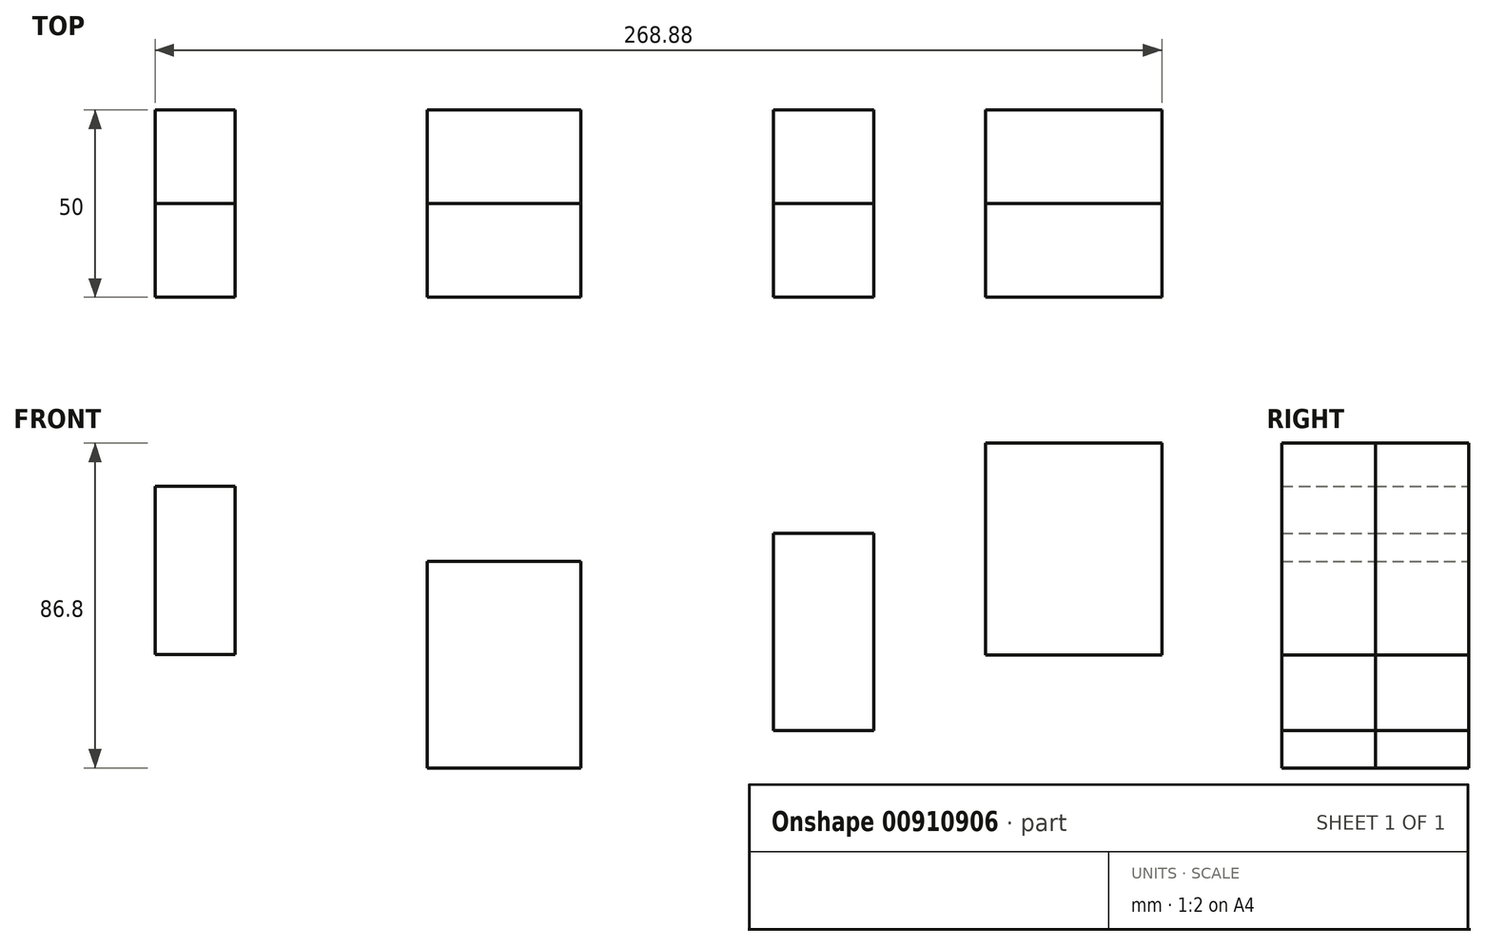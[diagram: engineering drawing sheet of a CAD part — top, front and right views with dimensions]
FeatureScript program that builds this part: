
annotation { "Feature Type Name" : "Feature", "Feature Type Description" : "" }
export const myFeature = defineFeature(function(context is Context, id is Id, definition is map)
    precondition{}
    {
        {
            var Q0;
            Q0=qCreatedBy(makeId("Front.planeOp"),FACE);
            var sketch = newSketch(context, id + "F0", { "sketchPlane" : qUnion([Q0])});
            skLineSegment(sketch, "E0.bottom", {"start": v(-124.32, 42.1) * mm, "end": v(-102.93, 42.1) * mm});
            skLineSegment(sketch, "E0.top", {"start": v(-124.32, -2.77) * mm, "end": v(-102.93, -2.77) * mm});
            skLineSegment(sketch, "E0.left", {"start": v(-124.32, 42.1) * mm, "end": v(-124.32, -2.77) * mm});
            skLineSegment(sketch, "E0.right", {"start": v(-102.93, 42.1) * mm, "end": v(-102.93, -2.77) * mm});
            skLineSegment(sketch, "E1.bottom", {"start": v(-51.6, 22.03) * mm, "end": v(-10.55, 22.03) * mm});
            skLineSegment(sketch, "E1.top", {"start": v(-51.6, -33.13) * mm, "end": v(-10.55, -33.13) * mm});
            skLineSegment(sketch, "E1.left", {"start": v(-51.6, 22.03) * mm, "end": v(-51.6, -33.13) * mm});
            skLineSegment(sketch, "E1.right", {"start": v(-10.55, 22.03) * mm, "end": v(-10.55, -33.13) * mm});
            skLineSegment(sketch, "E2.bottom", {"start": v(40.77, 29.6) * mm, "end": v(67.58, 29.6) * mm});
            skLineSegment(sketch, "E2.top", {"start": v(40.77, -23.12) * mm, "end": v(67.58, -23.12) * mm});
            skLineSegment(sketch, "E2.left", {"start": v(40.77, 29.6) * mm, "end": v(40.77, -23.12) * mm});
            skLineSegment(sketch, "E2.right", {"start": v(67.58, 29.6) * mm, "end": v(67.58, -23.12) * mm});
            skLineSegment(sketch, "E3.bottom", {"start": v(97.52, 53.67) * mm, "end": v(144.56, 53.67) * mm});
            skLineSegment(sketch, "E3.top", {"start": v(97.52, -2.9) * mm, "end": v(144.56, -2.9) * mm});
            skLineSegment(sketch, "E3.left", {"start": v(97.52, 53.67) * mm, "end": v(97.52, -2.9) * mm});
            skLineSegment(sketch, "E3.right", {"start": v(144.56, 53.67) * mm, "end": v(144.56, -2.9) * mm});
            skSolve(sketch);
        }
        {
            var Q0;
            Q0 = qSketchRegion(id + "F0", true);
            extrude(context, id + "F1", {"entities" : qUnion([Q0]), "depth" : 25 * mm, "offsetDistance" : 25 * mm});
        }
        {
            var Q0;
            Q0=makeQuery(id+"F1.opExtrude","CAP_FACE",FACE,{"disambiguationData":[OSD([sQuery(id+"F0.wireOp",EDGE,"E0.bottom"),sQuery(id+"F0.wireOp",EDGE,"E0.top"),sQuery(id+"F0.wireOp",EDGE,"E0.left"),sQuery(id+"F0.wireOp",EDGE,"E0.right")])],"isStart":false});
            var Q1;
            Q1=makeQuery(id+"F1.opExtrude","CAP_FACE",FACE,{"disambiguationData":[OSD([sQuery(id+"F0.wireOp",EDGE,"E1.bottom"),sQuery(id+"F0.wireOp",EDGE,"E1.top"),sQuery(id+"F0.wireOp",EDGE,"E1.left"),sQuery(id+"F0.wireOp",EDGE,"E1.right")])],"isStart":false});
            var Q2;
            Q2=makeQuery(id+"F1.opExtrude","CAP_FACE",FACE,{"disambiguationData":[OSD([sQuery(id+"F0.wireOp",EDGE,"E2.bottom"),sQuery(id+"F0.wireOp",EDGE,"E2.top"),sQuery(id+"F0.wireOp",EDGE,"E2.left"),sQuery(id+"F0.wireOp",EDGE,"E2.right")])],"isStart":false});
            var Q3;
            Q3=makeQuery(id+"F1.opExtrude","CAP_FACE",FACE,{"disambiguationData":[OSD([sQuery(id+"F0.wireOp",EDGE,"E3.bottom"),sQuery(id+"F0.wireOp",EDGE,"E3.top"),sQuery(id+"F0.wireOp",EDGE,"E3.left"),sQuery(id+"F0.wireOp",EDGE,"E3.right")])],"isStart":false});
            extrude(context, id + "F2", {"entities" : qUnion([Q0, Q1, Q2, Q3]), "depth" : 25 * mm, "offsetDistance" : 25 * mm});
        }
    });
